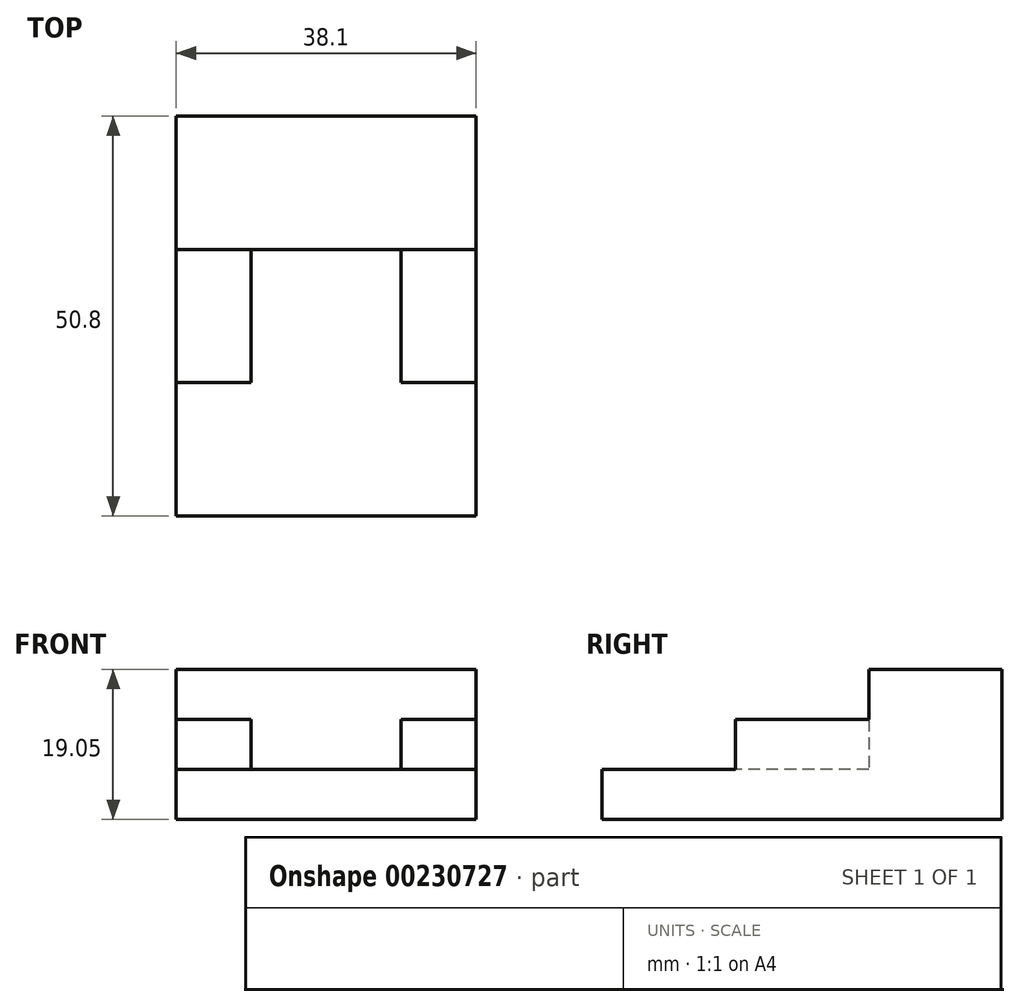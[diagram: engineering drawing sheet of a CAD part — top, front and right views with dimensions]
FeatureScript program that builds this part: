
annotation { "Feature Type Name" : "Feature", "Feature Type Description" : "" }
export const myFeature = defineFeature(function(context is Context, id is Id, definition is map)
    precondition{}
    {
        {
            var Q0;
            Q0=qCreatedBy(makeId("Top.planeOp"),FACE);
            var sketch = newSketch(context, id + "F0", { "sketchPlane" : qUnion([Q0])});
            skLineSegment(sketch, "E0.bottom", {"start": v(-19.05, 25.4) * mm, "end": v(19.05, 25.4) * mm});
            skLineSegment(sketch, "E0.top", {"start": v(-19.05, -25.4) * mm, "end": v(19.05, -25.4) * mm});
            skLineSegment(sketch, "E0.left", {"start": v(-19.05, 25.4) * mm, "end": v(-19.05, -25.4) * mm});
            skLineSegment(sketch, "E0.right", {"start": v(19.05, 25.4) * mm, "end": v(19.05, -25.4) * mm});
            skPoint(sketch, "E0.middle", {"position": v(0, 0) * mm});
            skSolve(sketch);
        }
        {
            var Q0;
            Q0=makeQuery(id+"F0.imprint","IMPRINT",FACE,{"disambiguationData":[TD([[makeQuery(id+"F0.imprint","IMPRINT",EDGE,{"derivedFrom":sQuery(id+"F0.wireOp",EDGE,"E0.bottom")}),-1.0]])]});
            extrude(context, id + "F1", {"entities" : qUnion([Q0]), "depth" : 6.35 * mm});
        }
        {
            var Q0;
            Q0=makeQuery(id+"F1.opExtrude","CAP_FACE",FACE,{"disambiguationData":[OSD([sQuery(id+"F0.wireOp",EDGE,"E0.bottom"),sQuery(id+"F0.wireOp",EDGE,"E0.top"),sQuery(id+"F0.wireOp",EDGE,"E0.left"),sQuery(id+"F0.wireOp",EDGE,"E0.right")])],"isStart":false});
            var sketch = newSketch(context, id + "F2", { "sketchPlane" : qUnion([Q0])});
            skLineSegment(sketch, "E1.bottom", {"start": v(-19.05, 25.4) * mm, "end": v(19.05, 25.4) * mm});
            skLineSegment(sketch, "E1.top", {"start": v(-19.05, 8.47) * mm, "end": v(19.05, 8.47) * mm});
            skLineSegment(sketch, "E1.left", {"start": v(-19.05, 25.4) * mm, "end": v(-19.05, 8.47) * mm});
            skLineSegment(sketch, "E1.right", {"start": v(19.05, 25.4) * mm, "end": v(19.05, 8.47) * mm});
            skSolve(sketch);
        }
        {
            var Q0;
            Q0=makeQuery(id+"F2.imprint","IMPRINT",FACE,{"disambiguationData":[TD([[makeQuery(id+"F2.imprint","IMPRINT",EDGE,{"derivedFrom":sQuery(id+"F2.wireOp",EDGE,"E1.bottom")}),-1.0]])]});
            extrude(context, id + "F3", {"entities" : qUnion([Q0]), "operationType" : NewBodyOperationType.ADD, "depth" : 12.7 * mm});
        }
        {
            var Q0;
            Q0=makeQuery(id+"F1.opExtrude","CAP_FACE",FACE,{"disambiguationData":[OSD([sQuery(id+"F0.wireOp",EDGE,"E0.bottom"),sQuery(id+"F0.wireOp",EDGE,"E0.top"),sQuery(id+"F0.wireOp",EDGE,"E0.left"),sQuery(id+"F0.wireOp",EDGE,"E0.right")])],"isStart":false});
            var sketch = newSketch(context, id + "F4", { "sketchPlane" : qUnion([Q0])});
            skLineSegment(sketch, "E2.bottom", {"start": v(-19.05, 8.47) * mm, "end": v(-9.53, 8.47) * mm});
            skLineSegment(sketch, "E2.top", {"start": v(-19.05, -8.48) * mm, "end": v(-9.53, -8.48) * mm});
            skLineSegment(sketch, "E2.left", {"start": v(-19.05, 8.47) * mm, "end": v(-19.05, -8.48) * mm});
            skLineSegment(sketch, "E2.right", {"start": v(-9.53, 8.47) * mm, "end": v(-9.53, -8.48) * mm});
            skPoint(sketch, "E3.oppositeSnap0", {"position": v(19.05, -8.47) * mm});
            skLineSegment(sketch, "E3.bottom", {"start": v(19.05, 8.47) * mm, "end": v(9.53, 8.47) * mm});
            skLineSegment(sketch, "E3.top", {"start": v(19.05, -8.47) * mm, "end": v(9.53, -8.47) * mm});
            skLineSegment(sketch, "E3.left", {"start": v(19.05, 8.47) * mm, "end": v(19.05, -8.47) * mm});
            skLineSegment(sketch, "E3.right", {"start": v(9.53, 8.47) * mm, "end": v(9.53, -8.47) * mm});
            skSolve(sketch);
        }
        {
            var Q0;
            Q0=makeQuery(id+"F4.imprint","IMPRINT",FACE,{"disambiguationData":[TD([[makeQuery(id+"F4.imprint","IMPRINT",EDGE,{"derivedFrom":sQuery(id+"F4.wireOp",EDGE,"E2.bottom")}),-1.0]])]});
            var Q1;
            Q1=makeQuery(id+"F4.imprint","IMPRINT",FACE,{"disambiguationData":[TD([[makeQuery(id+"F4.imprint","IMPRINT",EDGE,{"derivedFrom":sQuery(id+"F4.wireOp",EDGE,"E3.bottom")}),-1.0]])]});
            extrude(context, id + "F5", {"entities" : qUnion([Q0, Q1]), "operationType" : NewBodyOperationType.ADD, "depth" : 6.35 * mm});
        }
    });
